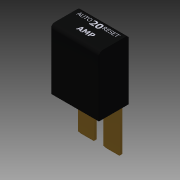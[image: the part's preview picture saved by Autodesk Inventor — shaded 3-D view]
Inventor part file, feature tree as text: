
AUTODESK INVENTOR PART (.ipt)
format: ipt  version: 2018 (Build 220112000, 112)  size: 453,632 bytes
history: native  units: in
note: dims shown in document units (in); Inventor stores cm internally (conversion verified against a paired STEP export)
features: sketch x6, extrude x4, plane x3, emboss x2, fillet x1, mirror x1
ambient origin geometry x8: Origin, YZ Plane, XZ Plane, XY Plane, X Axis, Y Axis, Z Axis, Center Point
bodies: Solid1 (feature_tree)
feature tree (17):
  extrude  "Extrusion1"  Depth=0.39in
  fillet  "Fillet1"  Radius=0.78in
  extrude  "Extrusion3"  Depth=0.212in
  extrude  "Extrusion4"  Depth=0.0585in
  extrude  "Extrusion5"  Depth=0.57in TaperAngle=0.0deg
  plane  "Work Plane1"
  mirror  "Mirror1"
  plane  "Work Plane2"
  emboss  "Emboss1"
  plane  "Work Plane4"
  emboss  "Emboss3"
  sketch  "Sketch1"  dims[d0=0.62in d1=0.39in d2=0.78in d3=0.0in]
  sketch  "Sketch2"  dims[d4=0.01in d5=0.05in d6=0.212in]
  sketch  "Sketch3"  dims[d8=0.031in d13=0.0585in]
  sketch  "Sketch4"  dims[d14=0.57in d15=0.0in d16=0.57in d17=0.0in]
  sketch  "Sketch6"  dims[d18=0.023in]
  sketch  "Sketch8"  dims[d19=0.023in d20=0.023in d21=0.57in d22=0.0in d26=0.1875in d27=0.0001in d28=0.0in d32=0.1875in d33=0.0001in d34=0.0in]
